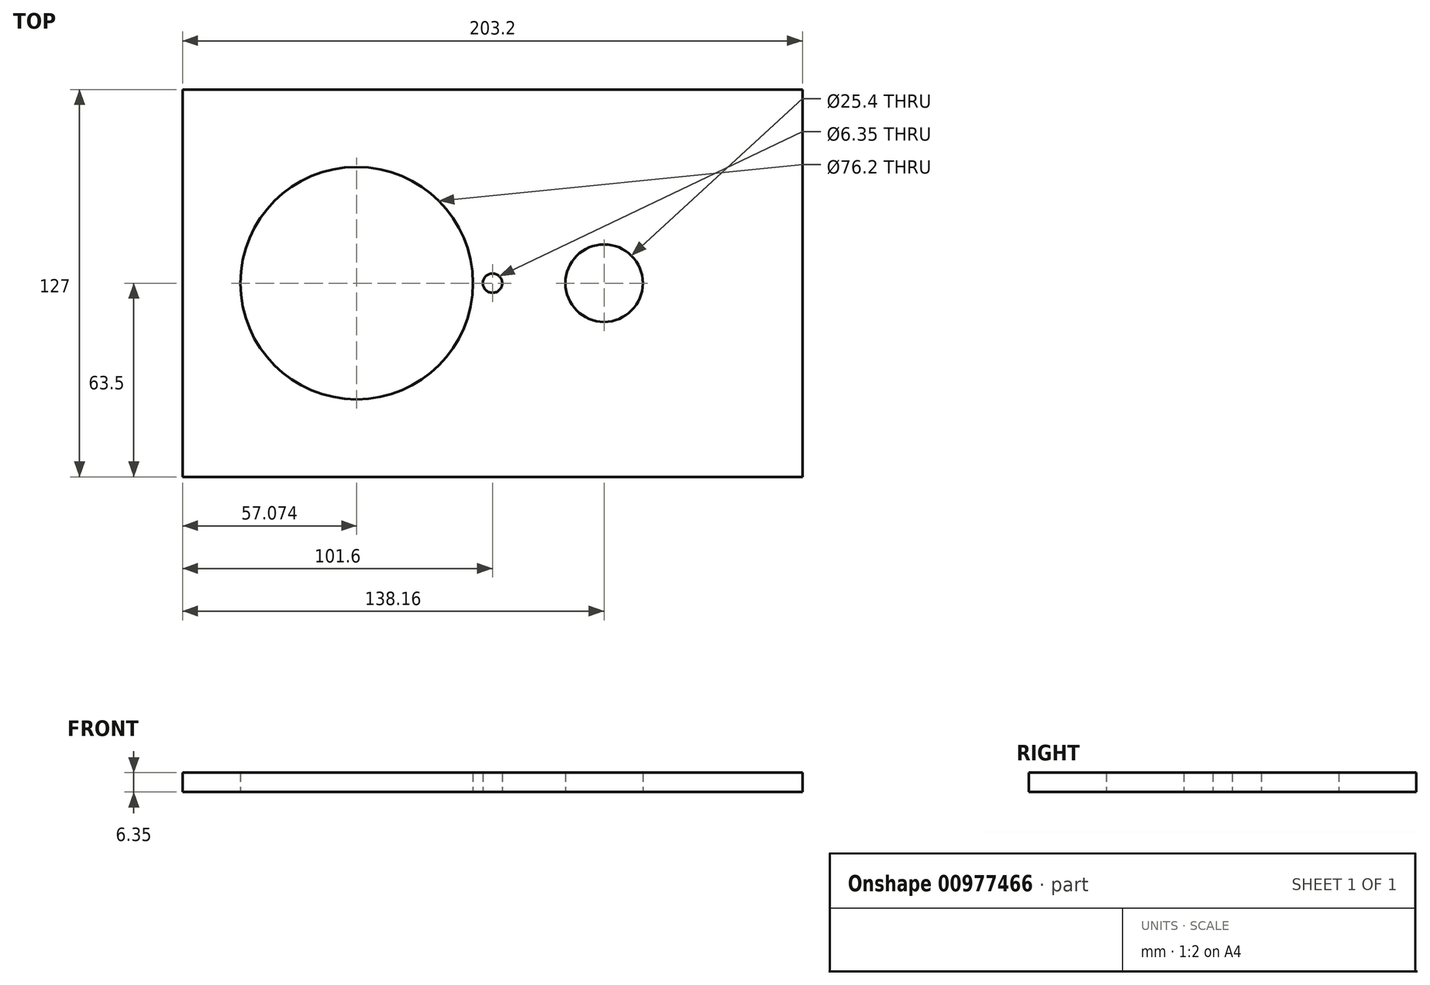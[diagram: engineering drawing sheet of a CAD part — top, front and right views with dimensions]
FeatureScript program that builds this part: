
annotation { "Feature Type Name" : "Feature", "Feature Type Description" : "" }
export const myFeature = defineFeature(function(context is Context, id is Id, definition is map)
    precondition{}
    {
        {
            var Q0;
            Q0=qCreatedBy(makeId("Top.planeOp"),FACE);
            var sketch = newSketch(context, id + "F0", { "sketchPlane" : qUnion([Q0])});
            skLineSegment(sketch, "E0.bottom", {"start": v(101.6, 63.5) * mm, "end": v(-101.6, 63.5) * mm});
            skLineSegment(sketch, "E0.top", {"start": v(101.6, -63.5) * mm, "end": v(-101.6, -63.5) * mm});
            skLineSegment(sketch, "E0.left", {"start": v(101.6, 63.5) * mm, "end": v(101.6, -63.5) * mm});
            skLineSegment(sketch, "E0.right", {"start": v(-101.6, 63.5) * mm, "end": v(-101.6, -63.5) * mm});
            skPoint(sketch, "E0.middle", {"position": v(0, 0) * mm});
            skCircle(sketch, "E1", {"center": v(0, 0) * mm, "radius": 3.18 * mm});
            skCircle(sketch, "E2", {"center": v(36.56, 0) * mm, "radius": 12.7 * mm});
            skCircle(sketch, "E3", {"center": v(-44.53, 0) * mm, "radius": 38.1 * mm});
            skSolve(sketch);
        }
        {
            var Q0;
            {var subQ0=sQuery(id+"F0.wireOp",EDGE,"E0.right");Q0=makeQuery(id+"F0.imprint","IMPRINT",FACE,{"disambiguationData":[TD([[makeQuery(id+"F0.imprint","IMPRINT",EDGE,{"derivedFrom":subQ0}),1.0]])]});}
            var Q1;
            {var subQ0=sQuery(id+"F0.wireOp",EDGE,"E0.left");Q1=makeQuery(id+"F0.imprint","IMPRINT",FACE,{"disambiguationData":[TD([[makeQuery(id+"F0.imprint","IMPRINT",EDGE,{"derivedFrom":subQ0}),-1.0]])]});}
            extrude(context, id + "F1", {"entities" : qUnion([Q0, Q1]), "depth" : 6.35 * mm, "offsetDistance" : 25.4 * mm});
        }
    });
